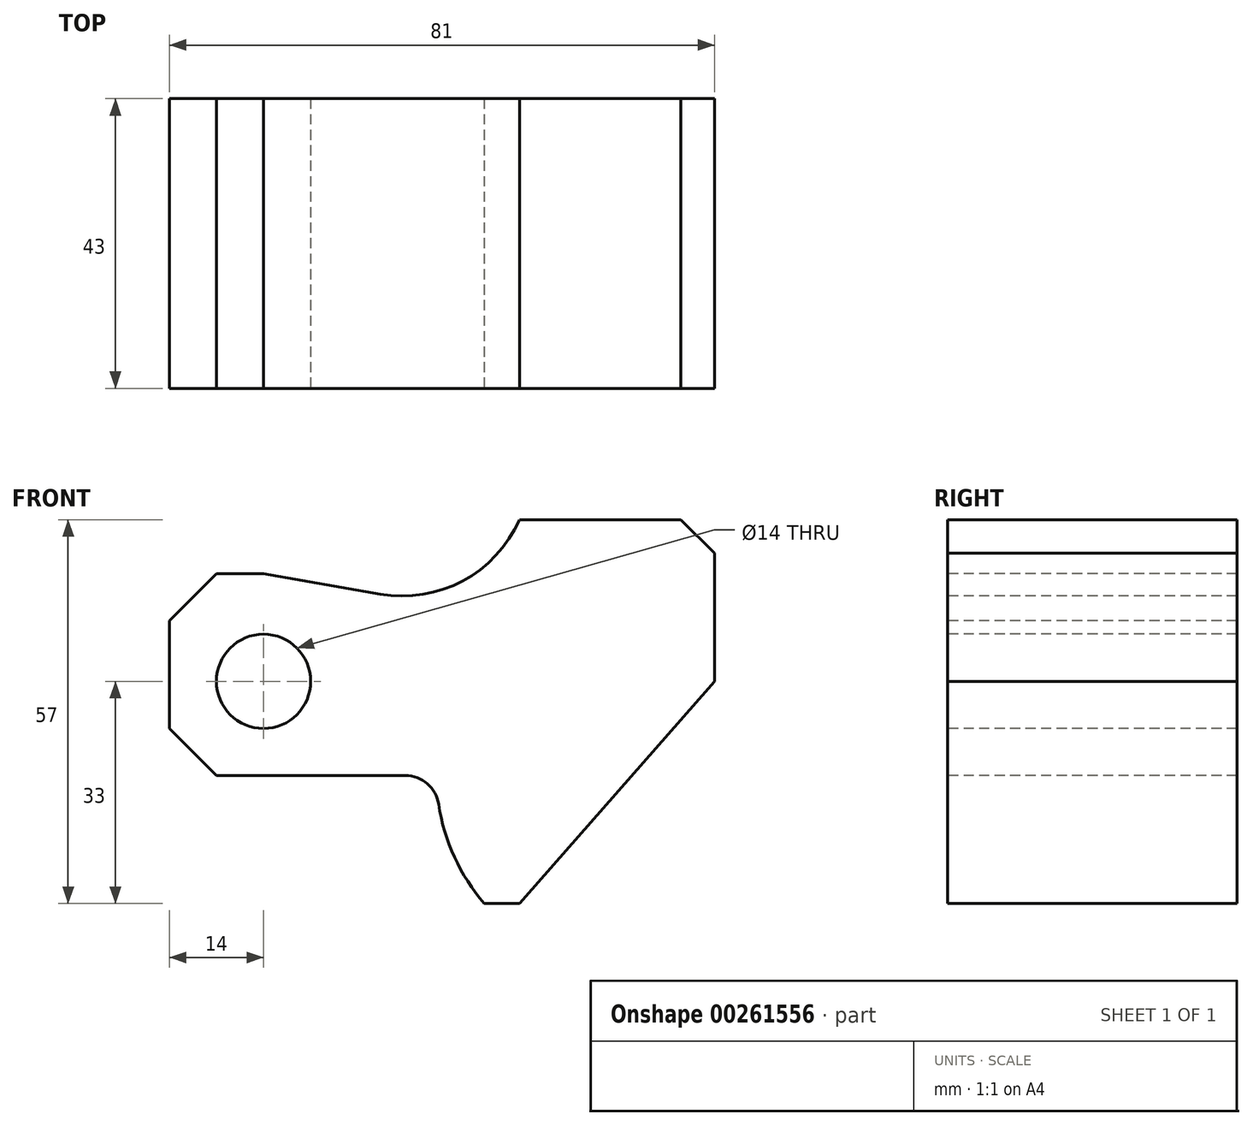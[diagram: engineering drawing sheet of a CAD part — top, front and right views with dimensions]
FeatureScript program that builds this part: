
annotation { "Feature Type Name" : "Feature", "Feature Type Description" : "" }
export const myFeature = defineFeature(function(context is Context, id is Id, definition is map)
    precondition{}
    {
        {
            var Q0;
            Q0=qCreatedBy(makeId("Front.planeOp"),FACE);
            var sketch = newSketch(context, id + "F0", { "sketchPlane" : qUnion([Q0])});
            skLineSegment(sketch, "E0.bottom", {"start": v(40.5, 28.5) * mm, "end": v(-40.5, 28.5) * mm});
            skLineSegment(sketch, "E0.top", {"start": v(40.5, -28.5) * mm, "end": v(-40.5, -28.5) * mm});
            skLineSegment(sketch, "E0.left", {"start": v(40.5, 28.5) * mm, "end": v(40.5, -28.5) * mm});
            skLineSegment(sketch, "E0.right", {"start": v(-40.5, 28.5) * mm, "end": v(-40.5, -28.5) * mm});
            skPoint(sketch, "E0.middle", {"position": v(0, 0) * mm});
            skPoint(sketch, "E1", {"position": v(40.5, 23.5) * mm});
            skPoint(sketch, "E2", {"position": v(40.5, 4.5) * mm});
            skPoint(sketch, "E3", {"position": v(-26.5, 4.5) * mm});
            skCircle(sketch, "E4", {"center": v(-26.5, 4.5) * mm, "radius": 7 * mm});
            skPoint(sketch, "E5", {"position": v(-26.5, -9.5) * mm});
            skPoint(sketch, "E6", {"position": v(-40.5, 20.5) * mm});
            skPoint(sketch, "E7", {"position": v(-40.5, -2.5) * mm});
            skPoint(sketch, "E8", {"position": v(-40.5, -9.5) * mm});
            skLineSegment(sketch, "E9", {"start": v(-40.5, -9.5) * mm, "end": v(-5.43, -9.5) * mm});
            skLineSegment(sketch, "E10", {"start": v(-40.5, -2.5) * mm, "end": v(-33.5, -9.5) * mm});
            skPoint(sketch, "E11", {"position": v(-40.5, 4.5) * mm});
            skPoint(sketch, "E12", {"position": v(-40.5, 13.5) * mm});
            skLineSegment(sketch, "E13", {"start": v(-40.5, 13.5) * mm, "end": v(-33.5, 20.5) * mm});
            skLineSegment(sketch, "E14", {"start": v(40.5, 23.5) * mm, "end": v(35.5, 28.5) * mm});
            skPoint(sketch, "E15", {"position": v(11.5, -28.5) * mm});
            skLineSegment(sketch, "E16", {"start": v(11.5, -28.5) * mm, "end": v(40.5, 4.5) * mm});
            skPoint(sketch, "E17", {"position": v(11.5, 28.5) * mm});
            skLineSegment(sketch, "E18", {"start": v(-40.5, 20.5) * mm, "end": v(-26.5, 20.5) * mm});
            skArc(sketch, "E19", {"start": v(-9.19, 17.45) * mm, "mid": v(3.07, 19.4) * mm, "end": v(11.5, 28.5) * mm});
            skLineSegment(sketch, "E20", {"start": v(-26.5, 20.5) * mm, "end": v(-9.19, 17.45) * mm});
            skPoint(sketch, "E21", {"position": v(28.2, -9.5) * mm});
            skArc(sketch, "E22", {"start": v(-0.49, -13.76) * mm, "mid": v(1.85, -21.62) * mm, "end": v(6.29, -28.5) * mm});
            skArc(sketch, "E23", {"start": v(-0.49, -13.76) * mm, "mid": v(-2.17, -10.71) * mm, "end": v(-5.43, -9.5) * mm});
            skSolve(sketch);
        }
        {
            var Q0;
            Q0=makeQuery(id+"F0.imprint","IMPRINT",FACE,{"disambiguationData":[TD([[makeQuery(id+"F0.imprint","IMPRINT",EDGE,{"derivedFrom":sQuery(id+"F0.wireOp",EDGE,"E4")}),-1.0]])]});
            extrude(context, id + "F1", {"entities" : qUnion([Q0]), "oppositeDirection" : true, "depth" : 43 * mm});
        }
    });
